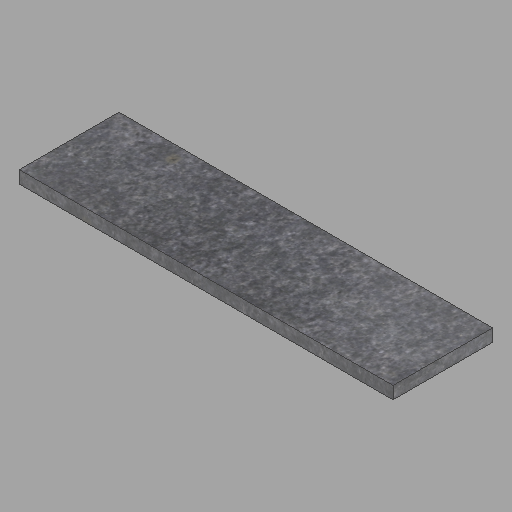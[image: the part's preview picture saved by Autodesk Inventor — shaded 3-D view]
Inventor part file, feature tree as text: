
AUTODESK INVENTOR PART (.ipt)
format: ipt  version: 2023 (Build 270158000, 158)  size: 192,512 bytes
history: native  units: in
note: dims shown in document units (in); Inventor stores cm internally (conversion verified against a paired STEP export)
features: other x1, extrude x1, sketch x1
ambient origin geometry x8: Origin, YZ Plane, XZ Plane, XY Plane, X Axis, Y Axis, Z Axis, Center Point
bodies: Solid1 (feature_tree)
feature tree (3):
  other  "2x16x60-12"
  extrude  "Extrusion1"  Depth=16.0in
  sketch  "Sketch1"  dims[d0=2.0in d1=16.0in d2=60.0in d3=0.0in]
